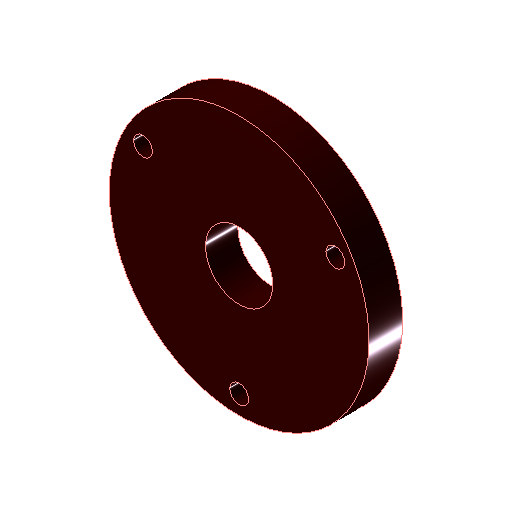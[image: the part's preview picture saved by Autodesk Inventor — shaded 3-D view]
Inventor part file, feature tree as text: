
AUTODESK INVENTOR PART (.ipt)
format: ipt  version: 2022 (Build 260153000, 153)  size: 127,488 bytes
history: native  units: mm
features: reference x7, other x3, sketch x2, revolve x1, extrude x1, projected_geometry x1
ambient origin geometry x8: Origin, YZ Plane, XZ Plane, XY Plane, X Axis, Y Axis, Z Axis, Center Point
bodies: Volumenkörper1 (feature_tree)
feature tree (15):
  revolve  "Umdrehung1"
  extrude  "Extrusion1"  Depth=12.65mm
  sketch  "Skizze1"  dims[d0=5.0mm d1=12.65mm]
  reference  "Referenz1"
  reference  "Referenz2"
  reference  "Referenz3"
  reference  "Referenz4"
  sketch  "Skizze2"  dims[d2=12.5mm d3=6.25mm d4=0.2mm d6=5.0mm d7=90.0deg d8=0.0mm d9=0.0mm]
  reference  "Referenz5"
  projected_geometry  "Projizierte Kontur1"
  reference  "Referenz6"
  reference  "Referenz7"
  other  "Assembly_ETL_v0.iam"
  other  "50_ETL_Base_v0:1"
  other  "50_ETL_28by_coil:1"
